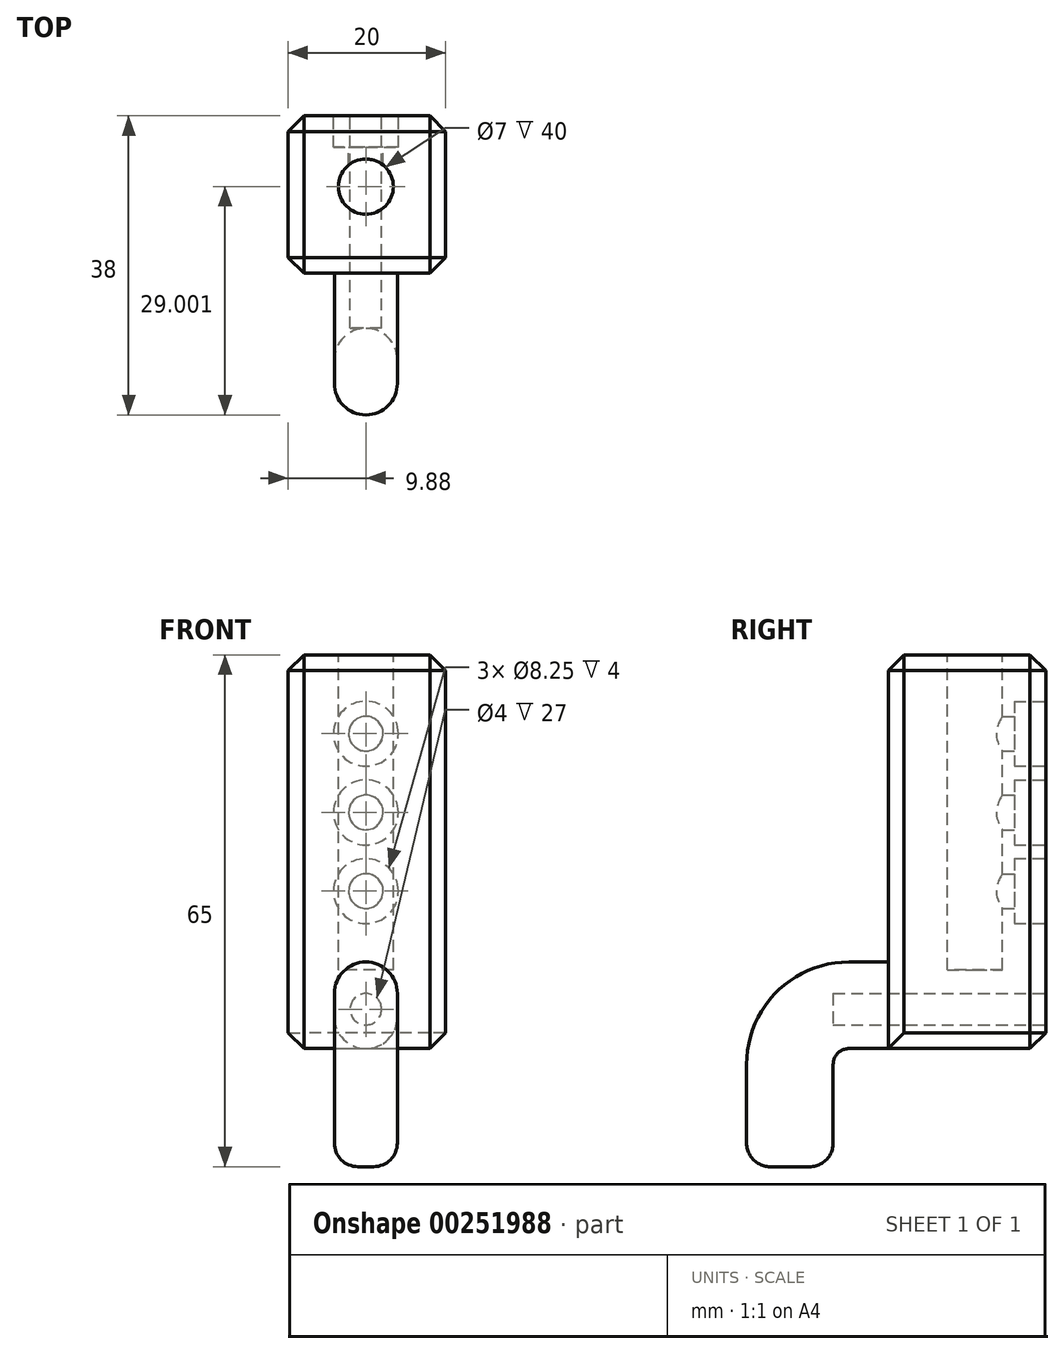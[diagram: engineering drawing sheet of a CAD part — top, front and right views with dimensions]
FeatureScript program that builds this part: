
annotation { "Feature Type Name" : "Feature", "Feature Type Description" : "" }
export const myFeature = defineFeature(function(context is Context, id is Id, definition is map)
    precondition{}
    {
        {
            var Q0;
            Q0=qCreatedBy(makeId("Top.planeOp"),FACE);
            var sketch = newSketch(context, id + "F0", { "sketchPlane" : qUnion([Q0])});
            skLineSegment(sketch, "E0.bottom", {"start": v(-9.88, 8.46) * mm, "end": v(10.12, 8.46) * mm});
            skLineSegment(sketch, "E0.top", {"start": v(-9.88, -11.54) * mm, "end": v(10.12, -11.54) * mm});
            skLineSegment(sketch, "E0.left", {"start": v(-9.88, 8.46) * mm, "end": v(-9.88, -11.54) * mm});
            skLineSegment(sketch, "E0.right", {"start": v(10.12, 8.46) * mm, "end": v(10.12, -11.54) * mm});
            skSolve(sketch);
        }
        {
            var Q0;
            Q0=makeQuery(id+"F0.imprint","IMPRINT",FACE,{"disambiguationData":[TD([[makeQuery(id+"F0.imprint","IMPRINT",EDGE,{"derivedFrom":sQuery(id+"F0.wireOp",EDGE,"E0.bottom")}),-1.0]])]});
            extrude(context, id + "F1", {"entities" : qUnion([Q0]), "depth" : 50 * mm});
        }
        {
            var Q0;
            Q0=makeQuery(id+"F1.opExtrude","SWEPT_FACE",FACE,{"disambiguationData":[OSD([sQuery(id+"F0.wireOp",EDGE,"E0.top")])]});
            var sketch = newSketch(context, id + "F2", { "sketchPlane" : qUnion([Q0])});
            skArc(sketch, "E1", {"start": v(-4, 4) * mm, "mid": v(0, 0) * mm, "end": v(4, 4) * mm});
            skArc(sketch, "E2", {"start": v(4, 7) * mm, "mid": v(0, 11) * mm, "end": v(-4, 7) * mm});
            skLineSegment(sketch, "E3", {"start": v(-4, 7) * mm, "end": v(-4, 4) * mm});
            skLineSegment(sketch, "E4", {"start": v(4, 7) * mm, "end": v(4, 4) * mm});
            skSolve(sketch);
        }
        {
            var Q0;
            Q0=qCreatedBy(makeId("Right.planeOp"),FACE);
            var sketch = newSketch(context, id + "F3", { "sketchPlane" : qUnion([Q0])});
            skLineSegment(sketch, "E5", {"start": v(-11.54, 0) * mm, "end": v(-16.54, 0) * mm});
            skLineSegment(sketch, "E6", {"start": v(-18.54, -2) * mm, "end": v(-18.54, -15) * mm});
            skPoint(sketch, "E7.visualSharp", {"position": v(-18.54, 0) * mm});
            skArc(sketch, "E7.filletArc", {"start": v(-16.54, 0) * mm, "mid": v(-17.95, -0.59) * mm, "end": v(-18.54, -2) * mm});
            skSolve(sketch);
        }
        {
            var Q0;
            Q0=makeQuery(id+"F2.imprint","IMPRINT",FACE,{"disambiguationData":[TD([[makeQuery(id+"F2.imprint","IMPRINT",EDGE,{"derivedFrom":sQuery(id+"F2.wireOp",EDGE,"E2")}),1.0]])]});
            var Q1;
            Q1=sQuery(id+"F3.wireOp",EDGE,"E5");
            var Q2;
            Q2=sQuery(id+"F3.wireOp",EDGE,"E7.filletArc");
            var Q3;
            Q3=sQuery(id+"F3.wireOp",EDGE,"E6");
            sweep(context, id + "F4", {"operationType" : NewBodyOperationType.ADD, "profiles" : qUnion([Q0]), "path" : qUnion([Q1, Q2, Q3])});
        }
        {
            var Q0;
            Q0=makeQuery(id+"F4.opSweep","CAP_FACE",FACE,{"disambiguationData":[OSD([sQuery(id+"F2.wireOp",EDGE,"E1"),sQuery(id+"F2.wireOp",EDGE,"E2"),sQuery(id+"F2.wireOp",EDGE,"E3"),sQuery(id+"F2.wireOp",EDGE,"E4"),sQuery(id+"F3.wireOp",VERTEX,"E6.end")])],"isStart":false});
            fillet(context, id + "F5", {"entities" : qUnion([Q0]), "radius" : 3 * mm, "tangentPropagation" : true, "allowEdgeOverflow" : false});
        }
        {
            var Q0;
            Q0=makeQuery(id+"F1.opExtrude","SWEPT_EDGE",EDGE,{"disambiguationData":[OSD([sQuery(id+"F0.wireOp",EDGE,"E0.top"),sQuery(id+"F0.wireOp",EDGE,"E0.right")])]});
            var Q1;
            Q1=makeQuery(id+"F1.opExtrude","SWEPT_EDGE",EDGE,{"disambiguationData":[OSD([sQuery(id+"F0.wireOp",EDGE,"E0.bottom"),sQuery(id+"F0.wireOp",EDGE,"E0.right")])]});
            var Q2;
            Q2=makeQuery(id+"F1.opExtrude","SWEPT_EDGE",EDGE,{"disambiguationData":[OSD([sQuery(id+"F0.wireOp",EDGE,"E0.top"),sQuery(id+"F0.wireOp",EDGE,"E0.left")])]});
            var Q3;
            Q3=makeQuery(id+"F1.opExtrude","CAP_EDGE",EDGE,{"disambiguationData":[OSD([sQuery(id+"F0.wireOp",EDGE,"E0.left")])],"isStart":true});
            var Q4;
            Q4=makeQuery(id+"F1.opExtrude","CAP_EDGE",EDGE,{"disambiguationData":[OSD([sQuery(id+"F0.wireOp",EDGE,"E0.right")])],"isStart":true});
            var Q5;
            Q5=makeQuery(id+"F1.opExtrude","CAP_EDGE",EDGE,{"disambiguationData":[OSD([sQuery(id+"F0.wireOp",EDGE,"E0.bottom")])],"isStart":true});
            var Q6;
            Q6=makeQuery(id+"F1.opExtrude","SWEPT_EDGE",EDGE,{"disambiguationData":[OSD([sQuery(id+"F0.wireOp",EDGE,"E0.bottom"),sQuery(id+"F0.wireOp",EDGE,"E0.left")])]});
            var Q7;
            Q7=makeQuery(id+"F1.opExtrude","CAP_FACE",FACE,{"disambiguationData":[OSD([sQuery(id+"F0.wireOp",EDGE,"E0.bottom"),sQuery(id+"F0.wireOp",EDGE,"E0.top"),sQuery(id+"F0.wireOp",EDGE,"E0.left"),sQuery(id+"F0.wireOp",EDGE,"E0.right")])],"isStart":false});
            chamfer(context, id + "F6", {"entities" : qUnion([Q0, Q1, Q2, Q3, Q4, Q5, Q6, Q7]), "width" : 2 * mm, "tangentPropagation" : true});
        }
        {
            var Q0;
            Q0=makeQuery(id+"F1.opExtrude","CAP_FACE",FACE,{"disambiguationData":[OSD([sQuery(id+"F0.wireOp",EDGE,"E0.bottom"),sQuery(id+"F0.wireOp",EDGE,"E0.top"),sQuery(id+"F0.wireOp",EDGE,"E0.left"),sQuery(id+"F0.wireOp",EDGE,"E0.right")])],"isStart":false});
            var sketch = newSketch(context, id + "F7", { "sketchPlane" : qUnion([Q0])});
            skCircle(sketch, "E8", {"center": v(0, -0.54) * mm, "radius": 3.5 * mm});
            skSolve(sketch);
        }
        {
            var Q0;
            Q0=makeQuery(id+"F7.imprint","IMPRINT",FACE,{"disambiguationData":[TD([[makeQuery(id+"F7.imprint","IMPRINT",EDGE,{"derivedFrom":sQuery(id+"F7.wireOp",EDGE,"E8")}),1.0]])]});
            extrude(context, id + "F8", {"entities" : qUnion([Q0]), "operationType" : NewBodyOperationType.REMOVE, "oppositeDirection" : true, "depth" : 40 * mm});
        }
        {
            var Q0;
            Q0=makeQuery(id+"F1.opExtrude","SWEPT_FACE",FACE,{"disambiguationData":[OSD([sQuery(id+"F0.wireOp",EDGE,"E0.bottom")])]});
            var sketch = newSketch(context, id + "F9", { "sketchPlane" : qUnion([Q0])});
            skPoint(sketch, "E9", {"position": v(0, 40) * mm});
            skPoint(sketch, "E10", {"position": v(0, 30) * mm});
            skPoint(sketch, "E11", {"position": v(0, 20) * mm});
            skSolve(sketch);
        }
        {
            var Q0;
            Q0=sQuery(id+"F9.wireOp",VERTEX,"E9");
            var Q1;
            Q1=sQuery(id+"F9.wireOp",VERTEX,"E10");
            var Q2;
            Q2=sQuery(id+"F9.wireOp",VERTEX,"E11");
            var Q3;
            Q3=makeQuery(id+"F1.opExtrude","SWEPT_BODY",BODY,{"disambiguationData":[OSD([sQuery(id+"F0.wireOp",EDGE,"E0.bottom"),sQuery(id+"F0.wireOp",EDGE,"E0.top"),sQuery(id+"F0.wireOp",EDGE,"E0.left"),sQuery(id+"F0.wireOp",EDGE,"E0.right")])]});
            hole(context, id + "F10", {"style" : HoleStyle.C_BORE, "endStyle" : HoleEndStyle.BLIND, "standardTappedOrClearance" : lookupTablePath({ "standard" : "ISO", "fit" : "Normal", "size" : "M4", "type" : "Clearance" }), "standardBlindInLast" : lookupTablePath({ "fit" : "Standard", "standard" : "ISO", "size" : "M4", "type" : "Clearance" }), "holeDiameter" : 4.4 * mm, "cBoreDiameter" : 8.25 * mm, "cBoreDepth" : 4 * mm, "holeDepth" : 10 * mm, "tappedDepth" : 12 * mm, "tapClearance" : 3, "locations" : qUnion([Q0, Q1, Q2]), "scope" : qUnion([Q3])});
        }
        {
            var Q0;
            Q0=makeQuery(id+"F1.opExtrude","SWEPT_FACE",FACE,{"disambiguationData":[OSD([sQuery(id+"F0.wireOp",EDGE,"E0.bottom")])]});
            var sketch = newSketch(context, id + "F11", { "sketchPlane" : qUnion([Q0])});
            skCircle(sketch, "E12", {"center": v(0, 5) * mm, "radius": 2 * mm});
            skSolve(sketch);
        }
        {
            var Q0;
            Q0=makeQuery(id+"F11.imprint","IMPRINT",FACE,{"disambiguationData":[TD([[makeQuery(id+"F11.imprint","IMPRINT",EDGE,{"derivedFrom":sQuery(id+"F11.wireOp",EDGE,"E12")}),1.0]])]});
            extrude(context, id + "F12", {"entities" : qUnion([Q0]), "operationType" : NewBodyOperationType.REMOVE, "oppositeDirection" : true, "depth" : 27 * mm});
        }
    });
